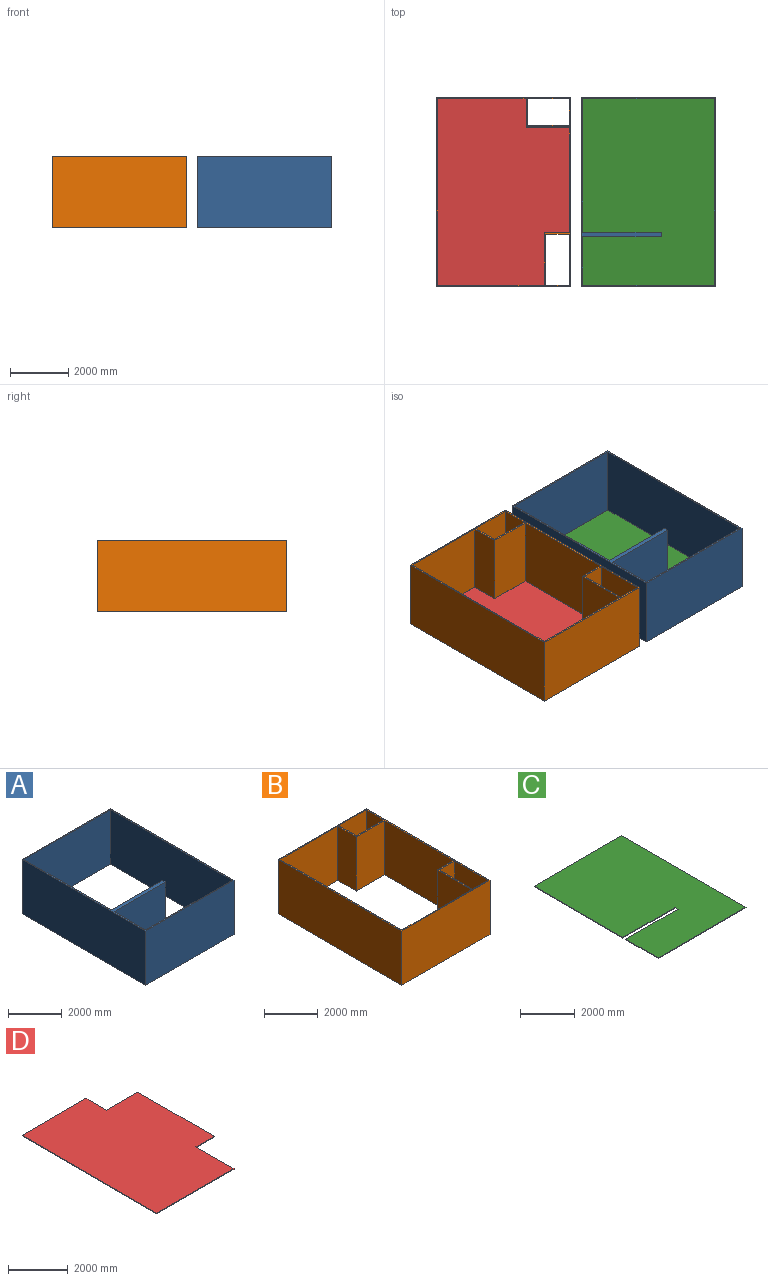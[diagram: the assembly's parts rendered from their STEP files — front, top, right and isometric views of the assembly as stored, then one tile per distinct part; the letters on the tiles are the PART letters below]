
ASSEMBLY  parts=4 mates=2
PART A: 14 faces, bbox 4622.8x6502.4x2463.8 mm
  f0: plane 4622.8x2463.8mm, normal (0,1,0), area 11389654.6mm2, adj f1,f11,f12,f13
  f1: plane 6502.4x2463.8mm, normal (-1,0,0), area 16020613.1mm2, adj f0,f2,f12,f13
  f2: plane 4622.8x2463.8mm, normal (0,-1,0), area 11389654.6mm2, adj f1,f11,f12,f13
  f3: plane 2463.8x1670.05mm, normal (1,0,0), area 4114669.2mm2, adj f4,f10,f12,f13
  f4: plane 2692.4x2463.8mm, normal (0,-1,0), area 6633535.1mm2, adj f3,f5,f12,f13
  f5: plane 2463.8x152.4mm, normal (1,0,0), area 375483.1mm2, adj f4,f6,f12,f13
  f6: plane 2692.4x2463.8mm, normal (0,1,0), area 6633535.1mm2, adj f5,f7,f12,f13
  f7: plane 4578.35x2463.8mm, normal (1,0,0), area 11280138.7mm2, adj f6,f8,f12,f13
  f8: plane 4521.2x2463.8mm, normal (0,-1,0), area 11139332.6mm2, adj f7,f9,f12,f13
  f9: plane 6400.8x2463.8mm, normal (-1,0,0), area 15770291mm2, adj f8,f10,f12,f13
  f10: plane 4521.2x2463.8mm, normal (0,1,0), area 11139332.6mm2, adj f3,f9,f12,f13
  f11: plane 6502.4x2463.8mm, normal (1,0,0), area 16020613.1mm2, adj f0,f2,f12,f13
  f12: plane 6502.4x4622.8mm, normal (0,0,-1), area 1530319.5mm2, adj f0,f1,f2,f3,f4,f5,f6,f7
  f13: plane 6502.4x4622.8mm, normal (0,0,1), area 1530319.5mm2, adj f0,f1,f2,f3,f4,f5,f6,f7
PART B: 22 faces, bbox 4622.8x6502.4x2463.8 mm
  f0: plane 2463.8x920.75mm, normal (-1,0,0), area 2268543.9mm2, adj f1,f19,f20,f21
  f1: plane 2463.8x1435.1mm, normal (0,1,0), area 3535799.4mm2, adj f0,f2,f20,f21
  f2: plane 2463.8x920.75mm, normal (1,0,0), area 2268543.8mm2, adj f1,f19,f20,f21
  f3: plane 4622.8x2463.8mm, normal (0,1,0), area 11389654.6mm2, adj f4,f16,f20,f21
  f4: plane 6502.4x2463.8mm, normal (-1,0,0), area 16020613.1mm2, adj f3,f5,f20,f21
  f5: plane 4622.8x2463.8mm, normal (0,-1,0), area 11389654.6mm2, adj f4,f16,f20,f21
  f6: plane 2463.8x812.8mm, normal (0,-1,0), area 2002576.6mm2, adj f7,f17,f20,f21
  f7: plane 2463.8x1752.6mm, normal (-1,0,0), area 4318055.9mm2, adj f6,f8,f20,f21
  f8: plane 2463.8x812.8mm, normal (0,1,0), area 2002576.6mm2, adj f7,f17,f20,f21
  f9: plane 2463.8x1485.9mm, normal (0,-1,0), area 3660960.4mm2, adj f10,f18,f20,f21
  f10: plane 3625.85x2463.8mm, normal (-1,0,0), area 8933369.2mm2, adj f9,f11,f20,f21
  f11: plane 2463.8x863.6mm, normal (0,1,0), area 2127737.7mm2, adj f10,f12,f20,f21
  f12: plane 2463.8x1803.4mm, normal (-1,0,0), area 4443216.9mm2, adj f11,f13,f20,f21
  f13: plane 3657.6x2463.8mm, normal (0,1,0), area 9011594.9mm2, adj f12,f14,f20,f21
  f14: plane 6400.8x2463.8mm, normal (1,0,0), area 15770291mm2, adj f13,f15,f20,f21
  f15: plane 3035.3x2463.8mm, normal (0,-1,0), area 7478372.1mm2, adj f14,f18,f20,f21
  f16: plane 6502.4x2463.8mm, normal (1,0,0), area 16020613.1mm2, adj f3,f5,f20,f21
  f17: plane 2463.8x1752.6mm, normal (1,0,0), area 4318055.9mm2, adj f6,f8,f20,f21
  f18: plane 2463.8x971.55mm, normal (-1,0,0), area 2393704.9mm2, adj f9,f15,f20,f21
  f19: plane 2463.8x1435.1mm, normal (0,-1,0), area 3535799.4mm2, adj f0,f2,f20,f21
  f20: plane 6502.4x4622.8mm, normal (0,0,-1), area 1375158.5mm2, adj f0,f1,f2,f3,f4,f5,f6,f7
  f21: plane 6502.4x4622.8mm, normal (0,0,1), area 1375158.5mm2, adj f0,f1,f2,f3,f4,f5,f6,f7
PART C: 10 faces, bbox 4521.2x6400.8x25.4 mm
  f0: plane 2692.4x25.4mm, normal (0,1,0), area 68387mm2, adj f1,f7,f8,f9
  f1: plane 1670.05x25.4mm, normal (-1,0,0), area 42419.3mm2, adj f0,f2,f8,f9
  f2: plane 4521.2x25.4mm, normal (0,-1,0), area 114838.5mm2, adj f1,f3,f8,f9
  f3: plane 6400.8x25.4mm, normal (1,0,0), area 162580.3mm2, adj f2,f4,f8,f9
  f4: plane 4521.2x25.4mm, normal (0,1,0), area 114838.5mm2, adj f3,f5,f8,f9
  f5: plane 4578.35x25.4mm, normal (-1,0,0), area 116290.1mm2, adj f4,f6,f8,f9
  f6: plane 2692.4x25.4mm, normal (0,-1,0), area 68387mm2, adj f5,f7,f8,f9
  f7: plane 152.4x25.4mm, normal (-1,0,0), area 3871mm2, adj f0,f6,f8,f9
  f8: plane 6400.8x4521.2mm, normal (0,0,-1), area 28528975.2mm2, adj f0,f1,f2,f3,f4,f5,f6,f7
  f9: plane 6400.8x4521.2mm, normal (0,0,1), area 28528975.2mm2, adj f0,f1,f2,f3,f4,f5,f6,f7
PART D: 10 faces, bbox 4521.2x6400.8x25.4 mm
  f0: plane 3625.85x25.4mm, normal (1,0,0), area 92096.6mm2, adj f1,f7,f8,f9
  f1: plane 1485.9x25.4mm, normal (0,1,0), area 37741.9mm2, adj f0,f2,f8,f9
  f2: plane 971.55x25.4mm, normal (1,0,0), area 24677.4mm2, adj f1,f3,f8,f9
  f3: plane 3035.3x25.4mm, normal (0,1,0), area 77096.6mm2, adj f2,f4,f8,f9
  f4: plane 6400.8x25.4mm, normal (-1,0,0), area 162580.3mm2, adj f3,f5,f8,f9
  f5: plane 3657.6x25.4mm, normal (0,-1,0), area 92903mm2, adj f4,f6,f8,f9
  f6: plane 1803.4x25.4mm, normal (1,0,0), area 45806.4mm2, adj f5,f7,f8,f9
  f7: plane 863.6x25.4mm, normal (0,-1,0), area 21935.4mm2, adj f0,f6,f8,f9
  f8: plane 6400.8x4521.2mm, normal (0,0,-1), area 25938254.6mm2, adj f0,f1,f2,f3,f4,f5,f6,f7
  f9: plane 6400.8x4521.2mm, normal (0,0,1), area 25938254.6mm2, adj f0,f1,f2,f3,f4,f5,f6,f7
PLACE A t=(-2311.4,3251.2,25.4)mm
PLACE B t=(-7289.8,3251.2,25.4)mm
PLACE C t=(-2311.4,3251.2,25.4)mm
PLACE D t=(-7289.8,3251.2,25.4)mm
MATE fastened B.f5 <-> A.f2  axis (0,-1,0) through (-4978.4,0,2463.8)mm
MATE parallel D.f8 <-> C.f8  axis (0,0,-1) through (-6515.1,5480.05,0)mm
